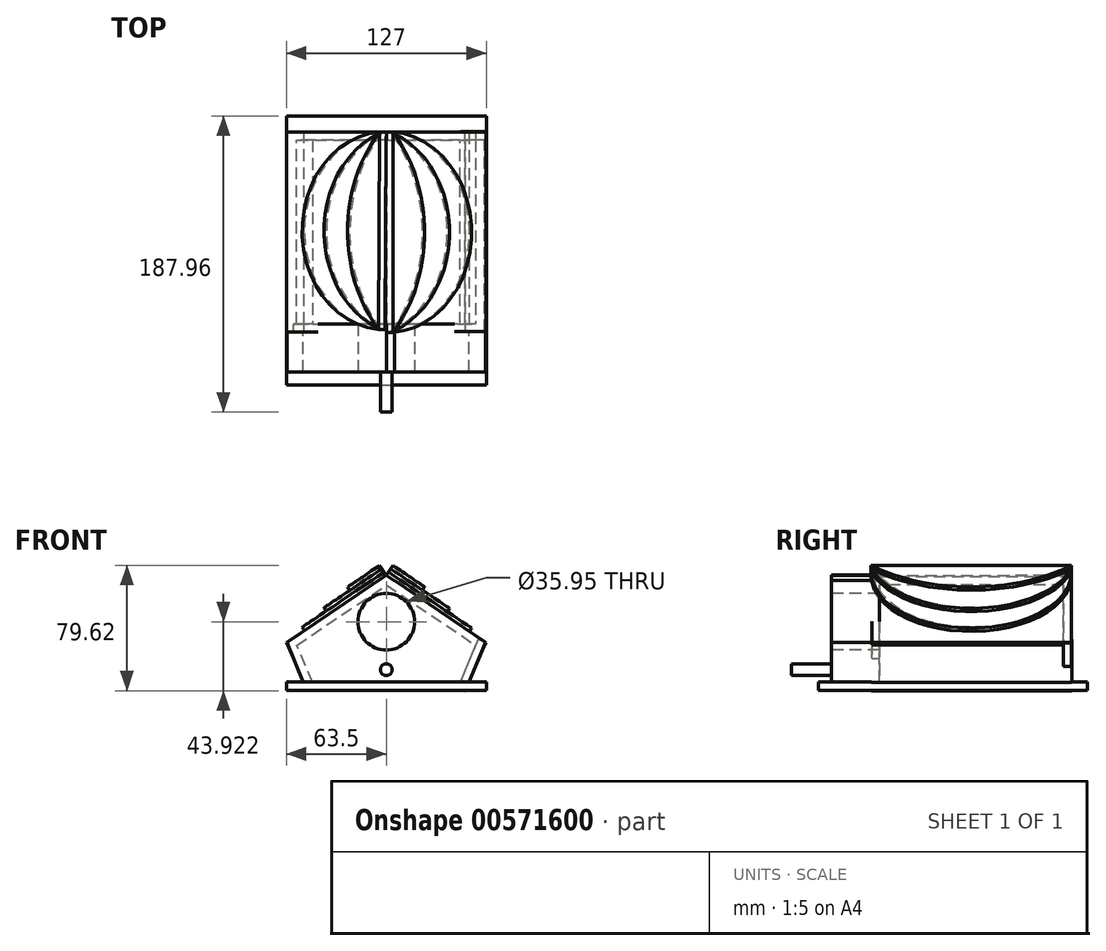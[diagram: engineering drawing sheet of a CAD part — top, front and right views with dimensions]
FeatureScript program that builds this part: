
annotation { "Feature Type Name" : "Feature", "Feature Type Description" : "" }
export const myFeature = defineFeature(function(context is Context, id is Id, definition is map)
    precondition{}
    {
        {
            var Q0;
            Q0=qCreatedBy(makeId("Top.planeOp"),FACE);
            var sketch = newSketch(context, id + "F0", { "sketchPlane" : qUnion([Q0])});
            skLineSegment(sketch, "E0.bottom", {"start": v(-63.5, 63.5) * mm, "end": v(63.5, 63.5) * mm});
            skLineSegment(sketch, "E0.top", {"start": v(-63.5, -63.5) * mm, "end": v(63.5, -63.5) * mm});
            skLineSegment(sketch, "E0.left", {"start": v(-63.5, 63.5) * mm, "end": v(-63.5, -63.5) * mm});
            skLineSegment(sketch, "E0.right", {"start": v(63.5, 63.5) * mm, "end": v(63.5, -63.5) * mm});
            skSolve(sketch);
        }
        {
            var Q0;
            Q0 = qSketchRegion(id + "F0", true);
            extrude(context, id + "F1", {"entities" : qUnion([Q0]), "depth" : 5.08 * mm, "offsetDistance" : 25.4 * mm});
        }
        {
            var Q0;
            Q0=makeQuery(id+"F1.opExtrude","SWEPT_FACE",FACE,{"disambiguationData":[OSD([sQuery(id+"F0.wireOp",EDGE,"E0.top")])]});
            var sketch = newSketch(context, id + "F2", { "sketchPlane" : qUnion([Q0])});
            skLineSegment(sketch, "E1", {"start": v(-62.94, 30.48) * mm, "end": v(0, 73.43) * mm});
            skLineSegment(sketch, "E2", {"start": v(0, 73.43) * mm, "end": v(62.94, 30.48) * mm});
            skLineSegment(sketch, "E3", {"start": v(62.94, 30.48) * mm, "end": v(50.36, 0) * mm});
            skLineSegment(sketch, "E4", {"start": v(50.36, 0) * mm, "end": v(-50.64, 0) * mm});
            skLineSegment(sketch, "E5", {"start": v(-50.64, 0) * mm, "end": v(-62.94, 30.48) * mm});
            skSolve(sketch);
        }
        {
            var Q0;
            {var subQ4=sQuery(id+"F2.wireOp",EDGE,"E1");Q0=makeQuery(id+"F2.imprint","IMPRINT",FACE,{"disambiguationData":[TD([[makeQuery(id+"F2.imprint","IMPRINT",EDGE,{"derivedFrom":subQ4}),-1.0]])]});}
            var Q1;
            {var subQ0=sQuery(id+"F2.wireOp",EDGE,"Nca5Ivi1-lNvX-X9Ft-Vkzw-ZzFuDkAyrcE6");var subQ1=sQuery(id+"F0.wireOp",EDGE,"E0.top");var subQ2=makeQuery(id+"F1.opExtrude","CAP_EDGE",EDGE,{"disambiguationData":[OSD([subQ1])],"isStart":true});var subQ3=makeQuery(id+"F2.imprint","INTERSECT",VERTEX,{"derivedFrom":[subQ2,subQ0]});Q1=makeQuery(id+"F2.imprint","IMPRINT",FACE,{"disambiguationData":[TD([[makeQuery(id+"F2.imprint","IMPRINT",EDGE,{"disambiguationData":[TD([[subQ3,-1.0]])],"derivedFrom":subQ0}),-1.0]])]});}
            extrude(context, id + "F3", {"entities" : qUnion([Q0, Q1]), "operationType" : NewBodyOperationType.ADD, "oppositeDirection" : true, "depth" : 5.08 * mm, "offsetDistance" : 25.4 * mm});
        }
        {
            var Q0;
            {var subQ0=sQuery(id+"F0.wireOp",EDGE,"E0.top");Q0=makeQuery(id+"FZ4zcoxZqnLx5GL_1.boolean.opBoolean","MERGE",FACE,{"derivedFrom":[makeQuery(id+"F3.boolean.opBoolean","MERGE",FACE,{"derivedFrom":[makeQuery(id+"F1.opExtrude","SWEPT_FACE",FACE,{"disambiguationData":[OSD([subQ0])]}),makeQuery(id+"F3.opExtrude","CAP_FACE",FACE,{"disambiguationData":[OSD([subQ0,sQuery(id+"F2.wireOp",EDGE,"Nca5Ivi1-lNvX-X9Ft-Vkzw-ZzFuDkAyrcE6"),sQuery(id+"F2.wireOp",EDGE,"E1"),sQuery(id+"F2.wireOp",EDGE,"E2"),sQuery(id+"F2.wireOp",EDGE,"3ywvDnwJ-mMuM-Snn5-wLAD-Rs0Pgs8Ub2uA")])],"isStart":true})]}),makeQuery(id+"FZ4zcoxZqnLx5GL_1.opExtrude","SWEPT_FACE",FACE,{"disambiguationData":[OSD([sQuery(id+"F20h28tRKLsYPAU_1.wireOp",EDGE,"E3ZWmYwf-ZCXB-H6l9-HYt9-AJ45HgzfRCNJ.right")])]})]});}
            var sketch = newSketch(context, id + "F4", { "sketchPlane" : qUnion([Q0])});
            skCircle(sketch, "E6", {"center": v(0, 13.15) * mm, "radius": 3.76 * mm});
            skSolve(sketch);
        }
        {
            var Q0;
            Q0 = qSketchRegion(id + "F4", true);
            extrude(context, id + "F5", {"entities" : qUnion([Q0]), "operationType" : NewBodyOperationType.ADD, "depth" : 50.8 * mm, "offsetDistance" : 25.4 * mm});
        }
        {
            var Q0;
            {var subQ0=sQuery(id+"F0.wireOp",EDGE,"E0.top");Q0=makeQuery(id+"FZ4zcoxZqnLx5GL_1.boolean.opBoolean","MERGE",FACE,{"derivedFrom":[makeQuery(id+"F3.boolean.opBoolean","MERGE",FACE,{"derivedFrom":[makeQuery(id+"F1.opExtrude","SWEPT_FACE",FACE,{"disambiguationData":[OSD([subQ0])]}),makeQuery(id+"F3.opExtrude","CAP_FACE",FACE,{"disambiguationData":[OSD([subQ0,sQuery(id+"F2.wireOp",EDGE,"Nca5Ivi1-lNvX-X9Ft-Vkzw-ZzFuDkAyrcE6"),sQuery(id+"F2.wireOp",EDGE,"E1"),sQuery(id+"F2.wireOp",EDGE,"E2"),sQuery(id+"F2.wireOp",EDGE,"3ywvDnwJ-mMuM-Snn5-wLAD-Rs0Pgs8Ub2uA")])],"isStart":true})]}),makeQuery(id+"FZ4zcoxZqnLx5GL_1.opExtrude","SWEPT_FACE",FACE,{"disambiguationData":[OSD([sQuery(id+"F20h28tRKLsYPAU_1.wireOp",EDGE,"E3ZWmYwf-ZCXB-H6l9-HYt9-AJ45HgzfRCNJ.right")])]})]});}
            var sketch = newSketch(context, id + "F6", { "sketchPlane" : qUnion([Q0])});
            skLineSegment(sketch, "E7.bottom", {"start": v(-63.5, 5.32) * mm, "end": v(63.5, 5.32) * mm});
            skLineSegment(sketch, "E7.top", {"start": v(-63.5, 0) * mm, "end": v(63.5, 0) * mm});
            skLineSegment(sketch, "E7.left", {"start": v(-63.5, 5.32) * mm, "end": v(-63.5, 0) * mm});
            skLineSegment(sketch, "E7.right", {"start": v(63.5, 5.32) * mm, "end": v(63.5, 0) * mm});
            skSolve(sketch);
        }
        {
            var Q0;
            Q0 = qSketchRegion(id + "F6", true);
            extrude(context, id + "F7", {"entities" : qUnion([Q0]), "operationType" : NewBodyOperationType.ADD, "depth" : 14.73 * mm, "offsetDistance" : 25.4 * mm});
        }
        {
            var Q0;
            Q0=makeQuery(id+"F1.opExtrude","SWEPT_FACE",FACE,{"disambiguationData":[OSD([sQuery(id+"F0.wireOp",EDGE,"E0.bottom")])]});
            var sketch = newSketch(context, id + "F8", { "sketchPlane" : qUnion([Q0])});
            skLineSegment(sketch, "E8", {"start": v(-63.22, 30.48) * mm, "end": v(-50.08, 0) * mm});
            skLineSegment(sketch, "E9", {"start": v(-50.08, 0) * mm, "end": v(0, 0) * mm});
            skLineSegment(sketch, "E10", {"start": v(-63.22, 30.48) * mm, "end": v(0, 73.02) * mm});
            skLineSegment(sketch, "E11.MirrorCS", {"start": v(63.22, 30.48) * mm, "end": v(0, 73.02) * mm});
            skLineSegment(sketch, "E12.MirrorCS", {"start": v(63.22, 30.48) * mm, "end": v(50.08, 0) * mm});
            skLineSegment(sketch, "E13.MirrorCS", {"start": v(50.08, 0) * mm, "end": v(0, 0) * mm});
            skSolve(sketch);
        }
        {
            var Q0;
            Q0 = qSketchRegion(id + "F8", true);
            extrude(context, id + "F9", {"entities" : qUnion([Q0]), "operationType" : NewBodyOperationType.ADD, "oppositeDirection" : true, "depth" : 5.08 * mm, "offsetDistance" : 25.4 * mm});
        }
        {
            var Q0;
            Q0=makeQuery(id+"F9.opExtrude","SWEPT_FACE",FACE,{"disambiguationData":[OSD([sQuery(id+"F8.wireOp",EDGE,"E12.MirrorCS")])]});
            var sketch = newSketch(context, id + "F10", { "sketchPlane" : qUnion([Q0])});
            skLineSegment(sketch, "E14.bottom", {"start": v(-63.5, 53.03) * mm, "end": v(63.25, 53.03) * mm});
            skLineSegment(sketch, "E14.top", {"start": v(-63.5, 20.27) * mm, "end": v(63.25, 20.27) * mm});
            skLineSegment(sketch, "E14.left", {"start": v(-63.5, 53.03) * mm, "end": v(-63.5, 20.27) * mm});
            skLineSegment(sketch, "E14.right", {"start": v(63.25, 53.03) * mm, "end": v(63.25, 20.27) * mm});
            skSolve(sketch);
        }
        {
            var Q0;
            Q0 = qSketchRegion(id + "F10", true);
            extrude(context, id + "F11", {"entities" : qUnion([Q0]), "operationType" : NewBodyOperationType.ADD, "oppositeDirection" : true, "depth" : 5.08 * mm, "offsetDistance" : 25.4 * mm});
        }
        {
            var Q0;
            Q0=makeQuery(id+"F3.opExtrude","SWEPT_FACE",FACE,{"disambiguationData":[OSD([sQuery(id+"F2.wireOp",EDGE,"E3")])]});
            var sketch = newSketch(context, id + "F12", { "sketchPlane" : qUnion([Q0])});
            skLineSegment(sketch, "E15.bottom", {"start": v(-63.5, 52.2) * mm, "end": v(63.76, 52.2) * mm});
            skLineSegment(sketch, "E15.top", {"start": v(-63.5, 18.91) * mm, "end": v(63.76, 18.91) * mm});
            skLineSegment(sketch, "E15.left", {"start": v(-63.5, 52.2) * mm, "end": v(-63.5, 18.91) * mm});
            skLineSegment(sketch, "E15.right", {"start": v(63.76, 52.2) * mm, "end": v(63.76, 18.91) * mm});
            skSolve(sketch);
        }
        {
            var Q0;
            Q0 = qSketchRegion(id + "F12", true);
            extrude(context, id + "F13", {"entities" : qUnion([Q0]), "operationType" : NewBodyOperationType.ADD, "oppositeDirection" : true, "depth" : 5.08 * mm, "offsetDistance" : 25.4 * mm});
        }
        {
            var Q0;
            Q0=makeQuery(id+"F9.opExtrude","SWEPT_FACE",FACE,{"disambiguationData":[OSD([sQuery(id+"F8.wireOp",EDGE,"E10")])]});
            var sketch = newSketch(context, id + "F14", { "sketchPlane" : qUnion([Q0])});
            skLineSegment(sketch, "E16.bottom", {"start": v(-40.76, 63.5) * mm, "end": v(35.53, 63.5) * mm});
            skLineSegment(sketch, "E16.top", {"start": v(-40.76, -63.11) * mm, "end": v(35.53, -63.11) * mm});
            skLineSegment(sketch, "E16.left", {"start": v(-40.76, 63.5) * mm, "end": v(-40.76, -63.11) * mm});
            skLineSegment(sketch, "E16.right", {"start": v(35.53, 63.5) * mm, "end": v(35.53, -63.11) * mm});
            skSolve(sketch);
        }
        {
            var Q0;
            Q0 = qSketchRegion(id + "F14", true);
            extrude(context, id + "F15", {"entities" : qUnion([Q0]), "operationType" : NewBodyOperationType.ADD, "oppositeDirection" : true, "depth" : 5.08 * mm, "offsetDistance" : 25.4 * mm});
        }
        {
            var Q0;
            Q0=makeQuery(id+"F9.opExtrude","SWEPT_FACE",FACE,{"disambiguationData":[OSD([sQuery(id+"F8.wireOp",EDGE,"E11.MirrorCS")])]});
            var sketch = newSketch(context, id + "F16", { "sketchPlane" : qUnion([Q0])});
            skLineSegment(sketch, "E17.bottom", {"start": v(-35.44, 63.5) * mm, "end": v(39.92, 63.5) * mm});
            skLineSegment(sketch, "E17.top", {"start": v(-35.44, -63.46) * mm, "end": v(39.92, -63.46) * mm});
            skLineSegment(sketch, "E17.left", {"start": v(-35.44, 63.5) * mm, "end": v(-35.44, -63.46) * mm});
            skLineSegment(sketch, "E17.right", {"start": v(39.92, 63.5) * mm, "end": v(39.92, -63.46) * mm});
            skSolve(sketch);
        }
        {
            var Q0;
            Q0 = qSketchRegion(id + "F16", true);
            extrude(context, id + "F17", {"entities" : qUnion([Q0]), "operationType" : NewBodyOperationType.ADD, "oppositeDirection" : true, "depth" : 5.08 * mm, "offsetDistance" : 25.4 * mm});
        }
        {
            var Q0;
            {var subQ0=sQuery(id+"F0.wireOp",EDGE,"E0.top");Q0=makeQuery(id+"F3.boolean.opBoolean","MERGE",FACE,{"derivedFrom":[makeQuery(id+"F1.opExtrude","SWEPT_FACE",FACE,{"disambiguationData":[OSD([subQ0])]}),makeQuery(id+"F3.opExtrude","CAP_FACE",FACE,{"disambiguationData":[OSD([subQ0,sQuery(id+"F2.wireOp",EDGE,"E1"),sQuery(id+"F2.wireOp",EDGE,"E2"),sQuery(id+"F2.wireOp",EDGE,"E3"),sQuery(id+"F2.wireOp",EDGE,"E5")])],"isStart":true})]});}
            var sketch = newSketch(context, id + "F18", { "sketchPlane" : qUnion([Q0])});
            skCircle(sketch, "E18", {"center": v(0, 43.64) * mm, "radius": 17.98 * mm});
            skSolve(sketch);
        }
        {
            var Q0;
            Q0 = qSketchRegion(id + "F18", true);
            extrude(context, id + "F19", {"entities" : qUnion([Q0]), "operationType" : NewBodyOperationType.REMOVE, "oppositeDirection" : true, "depth" : 43.69 * mm, "offsetDistance" : 25.4 * mm});
        }
        {
            var Q0;
            {var subQ0=sQuery(id+"F8.wireOp",EDGE,"E12.MirrorCS");var subQ2=sQuery(id+"F8.wireOp",EDGE,"E11.MirrorCS");var subQ4=sQuery(id+"F0.wireOp",EDGE,"E0.left");var subQ6=sQuery(id+"F0.wireOp",EDGE,"E0.bottom");var subQ10=sQuery(id+"F8.wireOp",EDGE,"E10");var subQ11=sQuery(id+"F8.wireOp",EDGE,"E8");Q0=makeQuery(id+"F15.boolean.opBoolean","MERGE",FACE,{"derivedFrom":[makeQuery(id+"F13.boolean.opBoolean","SPLIT",FACE,{"disambiguationData":[TD([makeQuery(id+"F1.opExtrude","SWEPT_FACE",FACE,{"disambiguationData":[OSD([subQ4])]})])],"derivedFrom":makeQuery(id+"F9.boolean.opBoolean","MERGE",FACE,{"derivedFrom":[makeQuery(id+"F1.opExtrude","SWEPT_FACE",FACE,{"disambiguationData":[OSD([subQ6])]}),makeQuery(id+"F9.opExtrude","CAP_FACE",FACE,{"disambiguationData":[OSD([subQ11,sQuery(id+"F8.wireOp",EDGE,"E9"),subQ10,subQ2,subQ0,sQuery(id+"F8.wireOp",EDGE,"E13.MirrorCS")])],"isStart":true})]})}),makeQuery(id+"F15.opExtrude","SWEPT_FACE",FACE,{"disambiguationData":[OSD([sQuery(id+"F14.wireOp",EDGE,"E16.bottom")])]})]});}
            var sketch = newSketch(context, id + "F20", { "sketchPlane" : qUnion([Q0])});
            skLineSegment(sketch, "E19.bottom", {"start": v(-63.5, 5.32) * mm, "end": v(63.5, 5.32) * mm});
            skLineSegment(sketch, "E19.top", {"start": v(-63.5, 0) * mm, "end": v(63.5, 0) * mm});
            skLineSegment(sketch, "E19.left", {"start": v(-63.5, 5.32) * mm, "end": v(-63.5, 0) * mm});
            skLineSegment(sketch, "E19.right", {"start": v(63.5, 5.32) * mm, "end": v(63.5, 0) * mm});
            skSolve(sketch);
        }
        {
            var Q0;
            Q0 = qSketchRegion(id + "F20", true);
            extrude(context, id + "F21", {"entities" : qUnion([Q0]), "operationType" : NewBodyOperationType.ADD, "depth" : 10.16 * mm, "offsetDistance" : 25.4 * mm});
        }
        {
            var Q0;
            Q0=makeQuery(id+"F15.boolean.opBoolean","MERGE",FACE,{"derivedFrom":[makeQuery(id+"F9.opExtrude","SWEPT_FACE",FACE,{"disambiguationData":[OSD([sQuery(id+"F8.wireOp",EDGE,"E10")])]}),makeQuery(id+"F15.opExtrude","CAP_FACE",FACE,{"disambiguationData":[OSD([sQuery(id+"F14.wireOp",EDGE,"E16.bottom"),sQuery(id+"F14.wireOp",EDGE,"E16.top"),sQuery(id+"F14.wireOp",EDGE,"E16.left"),sQuery(id+"F14.wireOp",EDGE,"E16.right")])],"isStart":true})]});
            var sketch = newSketch(context, id + "F22", { "sketchPlane" : qUnion([Q0])});
            skLineSegment(sketch, "E20", {"start": v(-40.76, 63.5) * mm, "end": v(-40.76, -63.81) * mm});
            skArc(sketch, "E21", {"start": v(-40.76, -63.81) * mm, "mid": v(22.9, -0.16) * mm, "end": v(-40.76, 63.5) * mm});
            skSolve(sketch);
        }
        {
            var Q0;
            Q0 = qSketchRegion(id + "F22", true);
            extrude(context, id + "F23", {"entities" : qUnion([Q0]), "operationType" : NewBodyOperationType.ADD, "depth" : 2.54 * mm, "offsetDistance" : 25.4 * mm});
        }
        {
            var Q0;
            Q0=makeQuery(id+"F17.boolean.opBoolean","MERGE",FACE,{"derivedFrom":[makeQuery(id+"F9.opExtrude","SWEPT_FACE",FACE,{"disambiguationData":[OSD([sQuery(id+"F8.wireOp",EDGE,"E11.MirrorCS")])]}),makeQuery(id+"F17.opExtrude","CAP_FACE",FACE,{"disambiguationData":[OSD([sQuery(id+"F16.wireOp",EDGE,"E17.bottom"),sQuery(id+"F16.wireOp",EDGE,"E17.top"),sQuery(id+"F16.wireOp",EDGE,"E17.left"),sQuery(id+"F16.wireOp",EDGE,"E17.right")])],"isStart":true})]});
            var sketch = newSketch(context, id + "F24", { "sketchPlane" : qUnion([Q0])});
            skArc(sketch, "E22", {"start": v(40.76, 63.5) * mm, "mid": v(-21.97, 1.2) * mm, "end": v(39.92, -61.95) * mm});
            skLineSegment(sketch, "E23", {"start": v(40.76, 63.5) * mm, "end": v(39.92, -61.95) * mm});
            skSolve(sketch);
        }
        {
            var Q0;
            Q0 = qSketchRegion(id + "F24", true);
            extrude(context, id + "F25", {"entities" : qUnion([Q0]), "operationType" : NewBodyOperationType.ADD, "depth" : 2.54 * mm, "offsetDistance" : 25.4 * mm});
        }
        {
            var Q0;
            Q0=makeQuery(id+"F23.opExtrude","CAP_FACE",FACE,{"disambiguationData":[OSD([sQuery(id+"F22.wireOp",EDGE,"E20"),sQuery(id+"F22.wireOp",EDGE,"E21")])],"isStart":false});
            var sketch = newSketch(context, id + "F26", { "sketchPlane" : qUnion([Q0])});
            skLineSegment(sketch, "E24", {"start": v(-40.76, 63.5) * mm, "end": v(-40.76, -63.81) * mm});
            skArc(sketch, "E25", {"start": v(-40.76, -63.81) * mm, "mid": v(4.3, -0.16) * mm, "end": v(-40.76, 63.5) * mm});
            skSolve(sketch);
        }
        {
            var Q0;
            Q0 = qSketchRegion(id + "F26", true);
            extrude(context, id + "F27", {"entities" : qUnion([Q0]), "operationType" : NewBodyOperationType.ADD, "depth" : 2.54 * mm, "offsetDistance" : 25.4 * mm});
        }
        {
            var Q0;
            Q0=makeQuery(id+"F25.opExtrude","CAP_FACE",FACE,{"disambiguationData":[OSD([sQuery(id+"F24.wireOp",EDGE,"E22"),sQuery(id+"F24.wireOp",EDGE,"E23")])],"isStart":false});
            var sketch = newSketch(context, id + "F28", { "sketchPlane" : qUnion([Q0])});
            skLineSegment(sketch, "E26", {"start": v(40.76, 63.5) * mm, "end": v(39.92, -61.95) * mm});
            skArc(sketch, "E27", {"start": v(40.76, 63.5) * mm, "mid": v(-3.5, 1.07) * mm, "end": v(39.92, -61.95) * mm});
            skSolve(sketch);
        }
        {
            var Q0;
            Q0 = qSketchRegion(id + "F28", true);
            extrude(context, id + "F29", {"entities" : qUnion([Q0]), "operationType" : NewBodyOperationType.ADD, "depth" : 2.54 * mm, "offsetDistance" : 25.4 * mm});
        }
        {
            var Q0;
            Q0=makeQuery(id+"F29.opExtrude","CAP_FACE",FACE,{"disambiguationData":[OSD([sQuery(id+"F28.wireOp",EDGE,"E26"),sQuery(id+"F28.wireOp",EDGE,"E27")])],"isStart":false});
            var sketch = newSketch(context, id + "F30", { "sketchPlane" : qUnion([Q0])});
            skLineSegment(sketch, "E28", {"start": v(40.76, 63.5) * mm, "end": v(39.92, -61.95) * mm});
            skArc(sketch, "E29", {"start": v(40.76, 63.5) * mm, "mid": v(16.18, 0.94) * mm, "end": v(39.92, -61.95) * mm});
            skSolve(sketch);
        }
        {
            var Q0;
            Q0 = qSketchRegion(id + "F30", true);
            extrude(context, id + "F31", {"entities" : qUnion([Q0]), "operationType" : NewBodyOperationType.ADD, "depth" : 2.54 * mm, "offsetDistance" : 25.4 * mm});
        }
        {
            var Q0;
            Q0=makeQuery(id+"F27.opExtrude","CAP_FACE",FACE,{"disambiguationData":[OSD([sQuery(id+"F26.wireOp",EDGE,"E24"),sQuery(id+"F26.wireOp",EDGE,"E25")])],"isStart":false});
            var sketch = newSketch(context, id + "F32", { "sketchPlane" : qUnion([Q0])});
            skLineSegment(sketch, "E30", {"start": v(-40.76, 63.5) * mm, "end": v(-40.76, -63.81) * mm});
            skArc(sketch, "E31", {"start": v(-40.76, -63.81) * mm, "mid": v(-16.45, -0.16) * mm, "end": v(-40.76, 63.5) * mm});
            skSolve(sketch);
        }
        {
            var Q0;
            Q0 = qSketchRegion(id + "F32", true);
            extrude(context, id + "F33", {"entities" : qUnion([Q0]), "operationType" : NewBodyOperationType.ADD, "depth" : 2.54 * mm, "offsetDistance" : 25.4 * mm});
        }
        {
            var Q0;
            {var subQ0=sQuery(id+"F0.wireOp",EDGE,"E0.top");Q0=makeQuery(id+"F3.boolean.opBoolean","MERGE",FACE,{"derivedFrom":[makeQuery(id+"F1.opExtrude","SWEPT_FACE",FACE,{"disambiguationData":[OSD([subQ0])]}),makeQuery(id+"F3.opExtrude","CAP_FACE",FACE,{"disambiguationData":[OSD([subQ0,sQuery(id+"F2.wireOp",EDGE,"E1"),sQuery(id+"F2.wireOp",EDGE,"E2"),sQuery(id+"F2.wireOp",EDGE,"E3"),sQuery(id+"F2.wireOp",EDGE,"E5")])],"isStart":true})]});}
            var sketch = newSketch(context, id + "F34", { "sketchPlane" : qUnion([Q0])});
            skSolve(sketch);
        }
        {
            var Q0;
            {var subQ4=sQuery(id+"F2.wireOp",EDGE,"E1");Q0=makeQuery(id+"F34.imprint","IMPRINT",FACE,{"disambiguationData":[TD([[makeQuery(id+"F34.imprint","IMPRINT",EDGE,{"derivedFrom":makeQuery(id+"F3.opExtrude","CAP_EDGE",EDGE,{"disambiguationData":[OSD([subQ4])],"isStart":true})}),-1.0]])]});}
            extrude(context, id + "F35", {"entities" : qUnion([Q0]), "operationType" : NewBodyOperationType.ADD, "depth" : 25.4 * mm, "offsetDistance" : 25.4 * mm});
        }
        {
            var Q0;
            Q0=makeQuery(id+"F7.opExtrude","CAP_FACE",FACE,{"disambiguationData":[OSD([sQuery(id+"F6.wireOp",EDGE,"E7.bottom"),sQuery(id+"F6.wireOp",EDGE,"E7.top"),sQuery(id+"F6.wireOp",EDGE,"E7.left"),sQuery(id+"F6.wireOp",EDGE,"E7.right")])],"isStart":false});
            var sketch = newSketch(context, id + "F36", { "sketchPlane" : qUnion([Q0])});
            skLineSegment(sketch, "E32.bottom", {"start": v(-63.5, 5.32) * mm, "end": v(63.5, 5.32) * mm});
            skLineSegment(sketch, "E32.top", {"start": v(-63.5, 0) * mm, "end": v(63.5, 0) * mm});
            skLineSegment(sketch, "E32.left", {"start": v(-63.5, 5.32) * mm, "end": v(-63.5, 0) * mm});
            skLineSegment(sketch, "E32.right", {"start": v(63.5, 5.32) * mm, "end": v(63.5, 0) * mm});
            skSolve(sketch);
        }
        {
            var Q0;
            Q0 = qSketchRegion(id + "F36", true);
            extrude(context, id + "F37", {"entities" : qUnion([Q0]), "operationType" : NewBodyOperationType.ADD, "depth" : 19.05 * mm, "offsetDistance" : 25.4 * mm});
        }
    });
